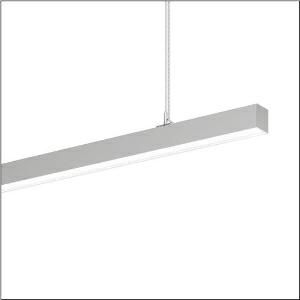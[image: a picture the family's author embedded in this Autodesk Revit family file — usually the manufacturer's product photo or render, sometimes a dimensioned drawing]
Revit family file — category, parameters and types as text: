
# Revit family: silica_r__21_51mx30dc49sb_4188
name_source: partatom
category: Lighting Fixtures
units: mm (PartAtom-declared; Revit-internal decimal feet)

## family parameters
Cut with Voids When Loaded = No
Host = Face
Light Source = No
Part Type = Normal
Room Calculation Point = No
Round Connector Dimension = Use Diameter
Shared = No

## types (1)
- --- (1 x LED, 10520 lm, 64.1 W, 4000K)
    Apparent Load = 64 VA
    CIE Flux Codes = 47 79 96 57 100
    Color Rendering = 80
    Color Temperature = 4000K
    Default Elevation = 1800 mm
    Description = Silica® 21, office luminaire, primary optical cover: cover, of PMMA, opal, light emission: direct/indirect distribution, primary light characteristic: symmetric, installation type: suspended mounting, LED, rated luminous flux: 10.520lm, luminous efficacy: 164lm/W, light colour: 840, colour temperature: 4000K, with terminal, 3+2-pole, max. 2.5mm², mains connection: 220..240V, AC, 50/60Hz, rated input power: 64.1W, luminaire housing, of aluminium, metallic grey (RAL 9006), length: 3.004mm, width: 53mm, height: 53mm, protection rating (complete): IP20, insulation class (complete): insulation class I (protective earthing), certification: CE, permissible operating ambient temperature: 0..+35°C, standard: EN 50419, packaging unit: 1 piece
    Height = 53 mm
    Lamp = 1 x LED
    Lamp Light Flux = 10520 lm
    Lamp Power = 64.1 W
    Lamp count = 1
    Length = 3004 mm
    Luminous efficacy = 164 lm/W
    Manufacturer = Siteco
    ModVariant = No
    Model = 51MX30DC49SB
    Mounting Place = Ceiling
    Mounting Type = Pendant
    Number of Poles = 1
    OnlyDefault = Yes
    Power Factor = 1
    Product Name = Silica® 21
    Product group = office luminaire | ceiling pendant
    ProductGroupID = 902
    Protection Class = Protection class I
    Protection Degree = IP 20
    RLX_Detail_Level = 1
    RLX_Emergency_Light_Flux = 0 lm
    RLX_Emergency_Type = 0
    RLX_Emergency_Type_DB = No
    RlxData = <blob elided: 23321 chars, md5=06cb8c39>
    Socket = socket
    Standby Power = 0 W
    System Light Flux = 10520 lm
    System Power = 64 W
    Type Comments = factory setting: luminous flux: 100 % | dim-lin: 254 | 218 mA
    Type Image = l_1297747.jpg
    URL = http://relux.com
    VarID = @adj_047143
    Voltage = 0 V
    Weight = 0.00 kg
    Width = 53 mm

## geometry (parser evidence)
native form markers: Blend x4, Sweep x12
no freeform markers — native parametric forms only
